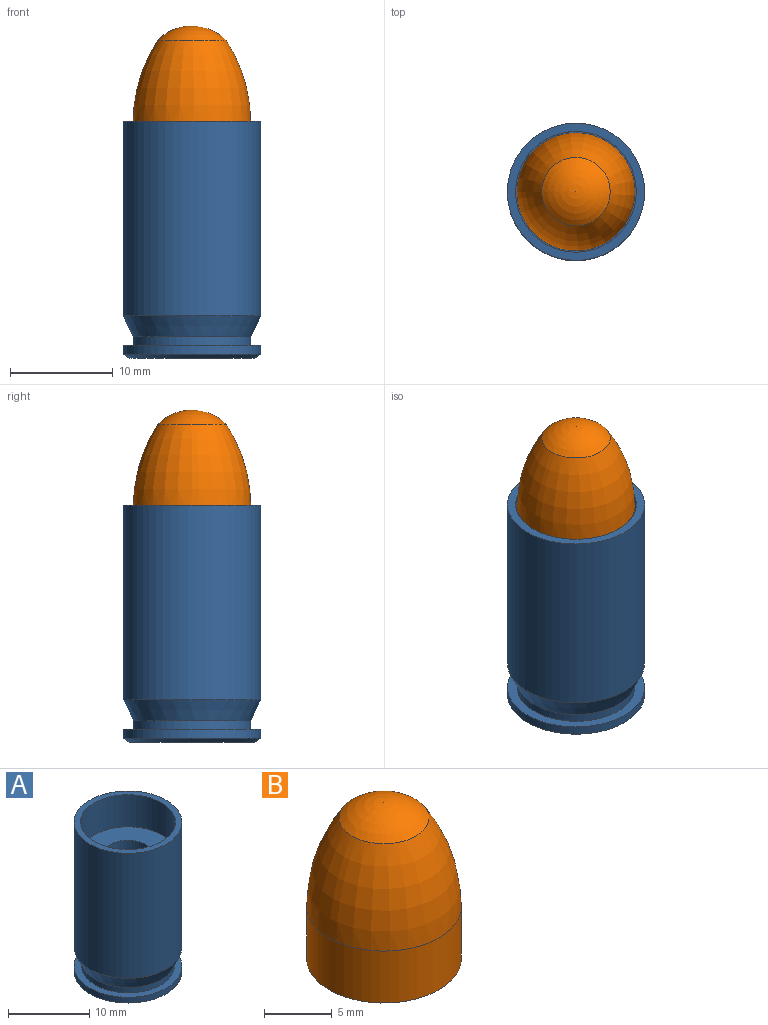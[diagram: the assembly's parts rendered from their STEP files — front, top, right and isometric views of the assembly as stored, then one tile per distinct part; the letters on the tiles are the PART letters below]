
ASSEMBLY  parts=2 mates=1
PART A: 11 faces, bbox 13.3x13.3x23 mm
  f0: cylinder r=3mm len=18.15mm, axis (0,0,1), area 342.1mm2, adj f1,f10
  f1: plane 11.73x11.73mm, normal (0,0,1), area 79.8mm2, adj f0,f2
  f2: cylinder r=5.87mm len=11.73mm, axis (0,0,1), area 178.7mm2, adj f1,f3
  f3: plane 13.33x13.33mm, normal (0,0,1), area 31.5mm2, adj f2,f4
  f4: cylinder r=6.67mm len=18.9mm, axis (0,0,1), area 791.5mm2, adj f3,f5
  f5: cone r=6.67mm half-angle=24.9deg, axis (0,0,1), area 87.9mm2, adj f4,f6
  f6: cylinder r=5.71mm len=11.43mm, axis (0,0,1), area 29.1mm2, adj f5,f7
  f7: plane 13.33x13.33mm, normal (0,0,1), area 36.9mm2, adj f6,f8
  f8: cylinder r=6.67mm len=13.33mm, axis (0,0,1), area 36mm2, adj f7,f9
  f9: cone r=6.67mm half-angle=55deg, axis (0,0,1), area 26.6mm2, adj f8,f10
  f10: plane 12.24x12.24mm, normal (0,0,-1), area 89.5mm2, adj f0,f9
PART B: 4 faces, bbox 11.4x11.4x14.1 mm
  f0: sphere r=4.7mm, area 40.7mm2, adj f1
  f1: revolved ~11.43x11.43mm, area 261.9mm2, adj f0,f2
  f2: cylinder r=5.71mm len=11.43mm, axis (0,0,-1), area 168.8mm2, adj f1,f3
  f3: plane 11.43x11.43mm, normal (0,0,-1), area 102.6mm2, adj f2
PLACE A t=(-8.15,-1.53,6.96)mm
PLACE B t=(-8.15,-1.53,6.81)mm
MATE fastened B.f2 <-> A.f0  axis (0,0,-1) through (-8.15,-1.53,11.42)mm
